# Revit family: P810029-020-30
name_source: partatom
category: Lighting Fixtures
units: mm (PartAtom-declared; Revit-internal decimal feet)

## family parameters
Cut with Voids When Loaded = No
Host = Face
Light Source = Yes
OmniClass Number = 23.80.70.11.14.17
OmniClass Title = Direct/Indirect
Part Type = Normal
Room Calculation Point = No
Round Connector Dimension = Use Diameter
Shared = Yes

## types (1)
- P810029-020-30
    Apparent Load = 16 VA
    Color Filter = 16777215
    Connector Description = Lighting Connector
    Default Elevation = 48 "
    Description = Intrinsic Collection 7” Antique Bronze Flush Mount LED Adjustable Eyeball
    Diameter = 7.25 "
    Dimming Lamp Color Temperature Shift = <None>
    Features = Illumination: The light can be adjusted to offer standard downlight, accent light, wall washer, or sloped ceiling light
An integrated ceiling pitch indicator makes adjusting the light to match the ceiling pitch easy.
Application: Elevate any room's design with the Intrinsic Collection 1-Light Antique Bronze Modern LED Surface Mount Eyeball Downlight ideal for any bathroom, bedroom, bonus room, bar, great room, kitchen, living room, work area, utility, or storeroom
suitable for residential and commercial applications.
Styles: Perfect for contemporary, modern, traditional, and transitional style settings.
Finish: Clean profile is coated in a handsome antique bronze finish.
Materials: Constructed from aluminum to ensure a long product lifespan
installation to a standard height junction box is made easy with the intuitive snap spring design.
15.8w dimmable LED is included, 3000K, 90CRI with 1000 delivered lumens.
Dimensions: Measures 7-1/4-inch diameter by 1-1/2-inch height.
Certifications: cCSAus damp location listed, ENERGY STAR qualified, meets California Title 24 JA8-2016.
Pairs With: Pairs with a variety of Progress Lighting fixtures.
Warranty: Our 5-Year Limited Warranty guarantees your complete satisfaction with your purchase and includes professional after-sales customer service support.
    Fixture distribution = Direct
    Glass = Paint - Hubbell - White Texture
    Gold = Hubbell - Gold
    Height = 1.5 "
    Housing Material = Paint - Hubbell - Textured Camera Black
    Lamp = LED
    Load Classification = Lighting
    Manufacturer = Progress Lighting
    Model = P810029-020-30
    Photometric Web File = PROG_P810029-020-30_20.01368_testlabreports.ies
    Power Factor = 1
    Product Documentation Link = https://hubbellcdn.com
    Product Link = https://www.hubbell.com
    Support = Paint - Hubbell - Light Silver
    Tilt Angle = -90.00°
    URL = https://www.hubbell.com
    Voltage = 120 V
    Warranty = 5 years Warranty
    Wattage Comments = 15.5W
    Watts = 16 W

## geometry (parser evidence)
native form markers: Sweep x2
no freeform markers — native parametric forms only
